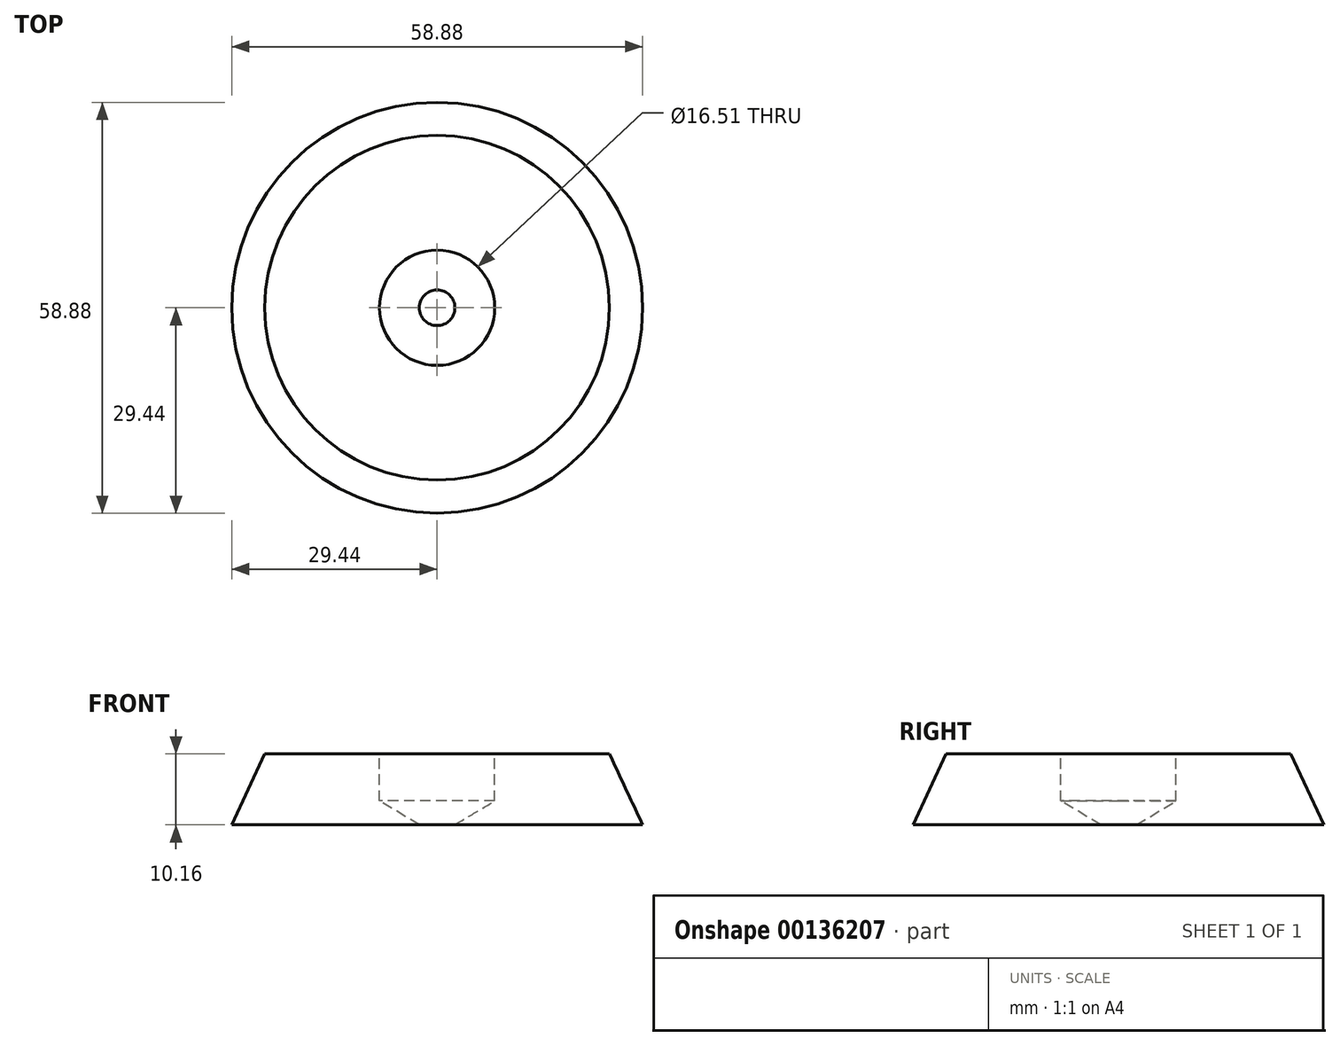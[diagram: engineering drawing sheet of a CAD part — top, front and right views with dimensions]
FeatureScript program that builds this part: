
annotation { "Feature Type Name" : "Feature", "Feature Type Description" : "" }
export const myFeature = defineFeature(function(context is Context, id is Id, definition is map)
    precondition{}
    {
        {
            var Q0;
            Q0=qCreatedBy(makeId("Top.planeOp"),FACE);
            var sketch = newSketch(context, id + "F0", { "sketchPlane" : qUnion([Q0])});
            skCircle(sketch, "E0", {"center": v(0, 0) * mm, "radius": 29.44 * mm});
            skSolve(sketch);
        }
        {
            var Q0;
            Q0 = qSketchRegion(id + "F0", true);
            extrude(context, id + "F1", {"entities" : qUnion([Q0]), "depth" : 10.16 * mm, "hasDraft" : true, "draftAngle" : 25 * degree, "draftPullDirection" : true});
        }
        {
            var Q0;
            Q0=makeQuery(id+"F1.opExtrude","CAP_FACE",FACE,{"disambiguationData":[OSD([sQuery(id+"F0.wireOp",EDGE,"E0")])],"isStart":false});
            var sketch = newSketch(context, id + "F2", { "sketchPlane" : qUnion([Q0])});
            skPoint(sketch, "E1", {"position": v(0, 0) * mm});
            skSolve(sketch);
        }
        {
            var Q0;
            Q0=sQuery(id+"F2.wireOp",VERTEX,"E1");
            var Q1;
            Q1=makeQuery(id+"F1.opExtrude","SWEPT_BODY",BODY,{"disambiguationData":[OSD([sQuery(id+"F0.wireOp",EDGE,"E0")])]});
            hole(context, id + "F3", {"style" : HoleStyle.SIMPLE, "endStyle" : HoleEndStyle.BLIND, "holeDiameter" : 16.5 * mm, "holeDepth" : 6.73 * mm, "locations" : qUnion([Q0]), "scope" : qUnion([Q1])});
        }
    });
